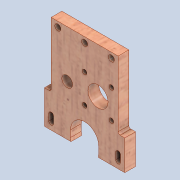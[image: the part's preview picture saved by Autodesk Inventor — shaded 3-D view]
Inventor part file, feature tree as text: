
AUTODESK INVENTOR PART (.ipt)
format: ipt  version: 2020 (Build 240168000, 168)  size: 327,168 bytes
history: native  units: mm
features: extrude x6, sketch x4, other x3, direct_edit x1, hole x1, fillet x1, reference x1, move_body x1
ambient origin geometry x8: Origin, YZ Plane, XZ Plane, XY Plane, X Axis, Y Axis, Z Axis, Center Point
bodies: Solid1 (feature_tree)
feature tree (18):
  extrude  "Extrusion1"  Depth=60.0mm
  extrude  "Extrusion4"  Depth=10.0mm TaperAngle=0.0deg
  extrude  "Extrusion5"  TaperAngle=0.0deg  [1 undecoded]
  extrude  "Extrusion6"  Depth=5.0mm
  extrude  "Extrusion7"  Depth=5.0mm
  extrude  "Extrusion8"  TaperAngle=0.0deg  [1 undecoded]
  direct_edit  "Direct Edit1"
  hole  "Hole1"  [1 undecoded]
  fillet  "Fillet1"  Radius=3.5mm
  sketch  "Sketch1"  dims[d0=60.0mm d1=65.0mm]
  sketch  "Sketch7"  dims[d2=8.0mm d3=0.0mm d11=10.0mm d12=0.0mm]
  reference  "Reference6"
  sketch  "Sketch8"  dims[d13=15.0mm d14=0.0mm d15=0.0mm]
  sketch  "Sketch9"  dims[d16=0.0mm d17=0.0mm d18=5.0mm d19=5.0mm d20=0.0mm d21=0.0mm d22=5.0mm d23=3.5mm d24=5.0mm d25=10.5mm d26=7.5mm d27=30.0mm d28=25.608627mm d29=20.0mm d31=21.5mm d33=3.5mm d35=8.0mm d36=17.0mm d37=27.469095mm d38=10.0mm d39=0.0mm d42=20.0mm d43=40.0mm d44=0.0mm d45=0.0mm d46=8.0mm d47=20.0mm d48=20.0mm d49=4.0mm d50=4.5mm d51=6.0mm d52=4.0mm d53=2.0mm d54=90.0deg d55=8.0mm d56=20.594885mm d57=1.5mm]
  parser-record x1  (decoder bookkeeping rows leaked as tree rows — omitted from the tree; the rows remain in map.json)
  other  "0005-00-00 Ansamblu_General.iam"
  other  "0005-10-002 Suport1 Seringa.ipt:8"
  move_body  "Move1"
note: 3 required parameter values undecoded (feature->parameter linkage not recoverable at this tier; creation-order binding heuristic only, values carry confidence <= 0.55)
note: 1 file-system path scrubbed to <path> (originals preserved in map.json)
